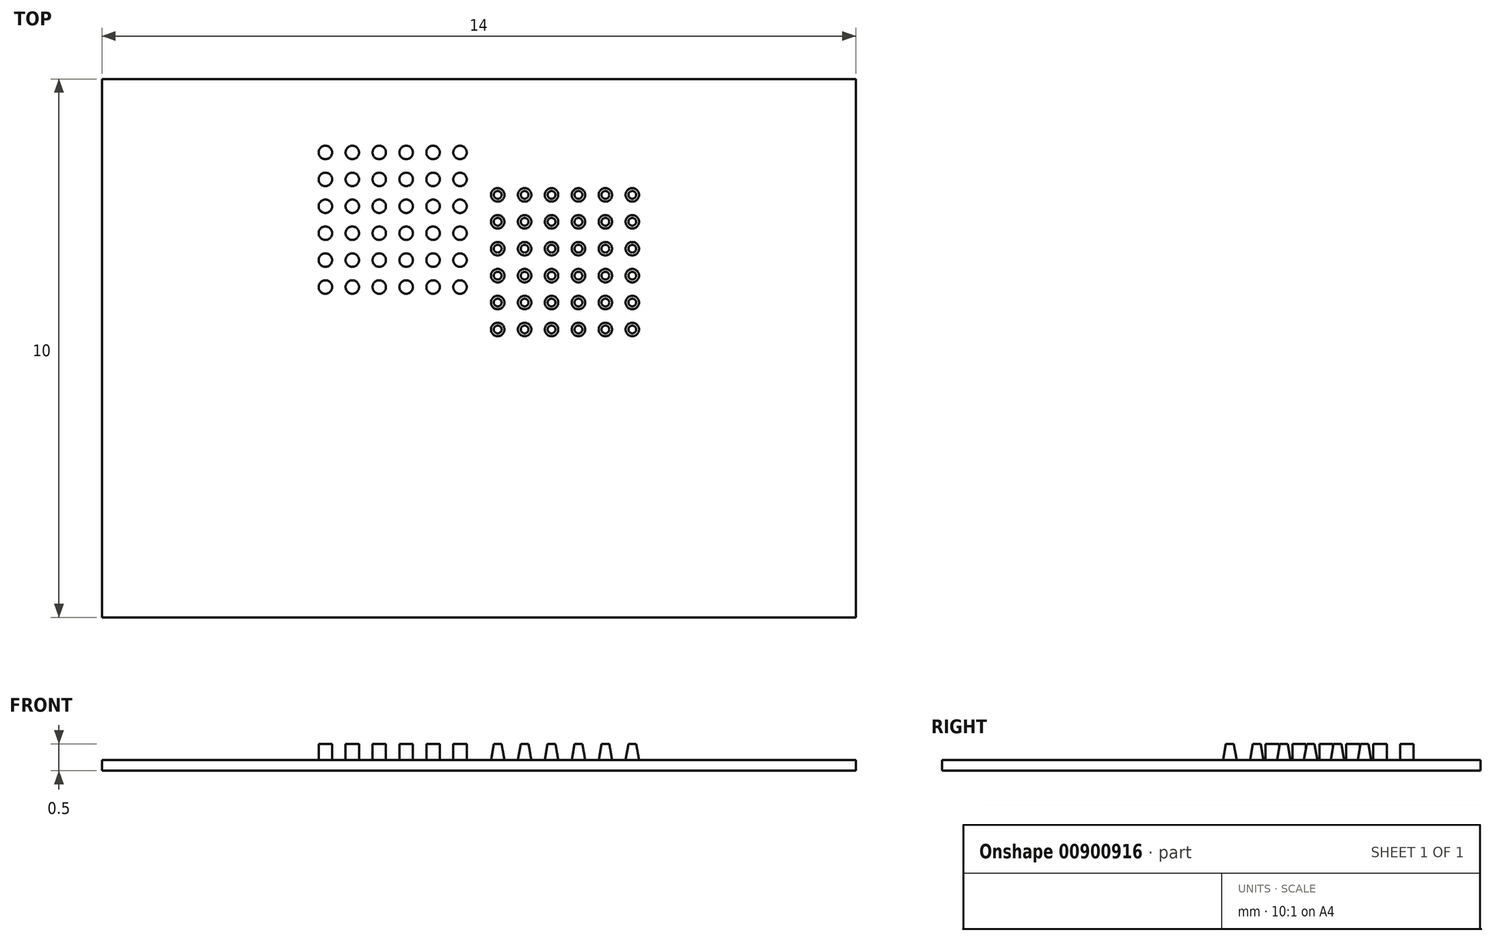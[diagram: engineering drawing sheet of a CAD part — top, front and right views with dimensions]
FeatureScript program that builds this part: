
annotation { "Feature Type Name" : "Feature", "Feature Type Description" : "" }
export const myFeature = defineFeature(function(context is Context, id is Id, definition is map)
    precondition{}
    {
        {
            var Q0;
            Q0=qCreatedBy(makeId("Top.planeOp"),FACE);
            var sketch = newSketch(context, id + "F0", { "sketchPlane" : qUnion([Q0])});
            skLineSegment(sketch, "E0.bottom", {"start": v(-7, -5) * mm, "end": v(7, -5) * mm});
            skLineSegment(sketch, "E0.top", {"start": v(-7, 5) * mm, "end": v(7, 5) * mm});
            skLineSegment(sketch, "E0.left", {"start": v(-7, -5) * mm, "end": v(-7, 5) * mm});
            skLineSegment(sketch, "E0.right", {"start": v(7, -5) * mm, "end": v(7, 5) * mm});
            skLineSegment(sketch, "E1", {"start": v(0, 5) * mm, "end": v(0, -5) * mm});
            skSolve(sketch);
        }
        {
            var Q0;
            Q0=qSketchRegion(id+"F0",true);
            extrude(context, id + "F1", {"entities" : qUnion([Q0]), "oppositeDirection" : true, "depth" : 0.2 * mm, "offsetDistance" : 25 * mm});
        }
        {
            var Q0;
            Q0=makeQuery(id+"F1.opExtrude","CAP_FACE",FACE,{"disambiguationData":[OSD([sQuery(id+"F0.wireOp",EDGE,"E0.bottom"),sQuery(id+"F0.wireOp",EDGE,"E0.top"),sQuery(id+"F0.wireOp",EDGE,"E0.left"),sQuery(id+"F0.wireOp",EDGE,"E0.right")])],"isStart":true});
            var sketch = newSketch(context, id + "F2", { "sketchPlane" : qUnion([Q0])});
            skCircle(sketch, "E2", {"center": v(-2.85, 1.14) * mm, "radius": 0.12 * mm});
            skCircle(sketch, "E3.0.1.0", {"center": v(-2.85, 1.64) * mm, "radius": 0.12 * mm});
            skCircle(sketch, "E3.0.2.0", {"center": v(-2.85, 2.14) * mm, "radius": 0.12 * mm});
            skCircle(sketch, "E3.0.3.0", {"center": v(-2.85, 2.64) * mm, "radius": 0.12 * mm});
            skCircle(sketch, "E3.0.4.0", {"center": v(-2.85, 3.14) * mm, "radius": 0.12 * mm});
            skCircle(sketch, "E3.0.5.0", {"center": v(-2.85, 3.64) * mm, "radius": 0.12 * mm});
            skCircle(sketch, "E3.1.0.0", {"center": v(-2.35, 1.14) * mm, "radius": 0.12 * mm});
            skCircle(sketch, "E3.1.1.0", {"center": v(-2.35, 1.64) * mm, "radius": 0.12 * mm});
            skCircle(sketch, "E3.1.2.0", {"center": v(-2.35, 2.14) * mm, "radius": 0.12 * mm});
            skCircle(sketch, "E3.1.3.0", {"center": v(-2.35, 2.64) * mm, "radius": 0.12 * mm});
            skCircle(sketch, "E3.1.4.0", {"center": v(-2.35, 3.14) * mm, "radius": 0.12 * mm});
            skCircle(sketch, "E3.1.5.0", {"center": v(-2.35, 3.64) * mm, "radius": 0.12 * mm});
            skCircle(sketch, "E3.2.0.0", {"center": v(-1.85, 1.14) * mm, "radius": 0.12 * mm});
            skCircle(sketch, "E3.2.1.0", {"center": v(-1.85, 1.64) * mm, "radius": 0.12 * mm});
            skCircle(sketch, "E3.2.2.0", {"center": v(-1.85, 2.14) * mm, "radius": 0.12 * mm});
            skCircle(sketch, "E3.2.3.0", {"center": v(-1.85, 2.64) * mm, "radius": 0.12 * mm});
            skCircle(sketch, "E3.2.4.0", {"center": v(-1.85, 3.14) * mm, "radius": 0.12 * mm});
            skCircle(sketch, "E3.2.5.0", {"center": v(-1.85, 3.64) * mm, "radius": 0.12 * mm});
            skCircle(sketch, "E3.3.0.0", {"center": v(-1.35, 1.14) * mm, "radius": 0.12 * mm});
            skCircle(sketch, "E3.3.1.0", {"center": v(-1.35, 1.64) * mm, "radius": 0.12 * mm});
            skCircle(sketch, "E3.3.2.0", {"center": v(-1.35, 2.14) * mm, "radius": 0.12 * mm});
            skCircle(sketch, "E3.3.3.0", {"center": v(-1.35, 2.64) * mm, "radius": 0.12 * mm});
            skCircle(sketch, "E3.3.4.0", {"center": v(-1.35, 3.14) * mm, "radius": 0.12 * mm});
            skCircle(sketch, "E3.3.5.0", {"center": v(-1.35, 3.64) * mm, "radius": 0.12 * mm});
            skCircle(sketch, "E3.4.0.0", {"center": v(-0.85, 1.14) * mm, "radius": 0.12 * mm});
            skCircle(sketch, "E3.4.1.0", {"center": v(-0.85, 1.64) * mm, "radius": 0.12 * mm});
            skCircle(sketch, "E3.4.2.0", {"center": v(-0.85, 2.14) * mm, "radius": 0.12 * mm});
            skCircle(sketch, "E3.4.3.0", {"center": v(-0.85, 2.64) * mm, "radius": 0.12 * mm});
            skCircle(sketch, "E3.4.4.0", {"center": v(-0.85, 3.14) * mm, "radius": 0.12 * mm});
            skCircle(sketch, "E3.4.5.0", {"center": v(-0.85, 3.64) * mm, "radius": 0.12 * mm});
            skCircle(sketch, "E3.5.0.0", {"center": v(-0.35, 1.14) * mm, "radius": 0.12 * mm});
            skCircle(sketch, "E3.5.1.0", {"center": v(-0.35, 1.64) * mm, "radius": 0.12 * mm});
            skCircle(sketch, "E3.5.2.0", {"center": v(-0.35, 2.14) * mm, "radius": 0.12 * mm});
            skCircle(sketch, "E3.5.3.0", {"center": v(-0.35, 2.64) * mm, "radius": 0.12 * mm});
            skCircle(sketch, "E3.5.4.0", {"center": v(-0.35, 3.14) * mm, "radius": 0.12 * mm});
            skCircle(sketch, "E3.5.5.0", {"center": v(-0.35, 3.64) * mm, "radius": 0.12 * mm});
            skLineSegment(sketch, "E3.direction1", {"start": v(-2.85, 1.14) * mm, "end": v(-2.35, 1.14) * mm, "construction": true});
            skLineSegment(sketch, "E3.direction2", {"start": v(-2.85, 1.14) * mm, "end": v(-2.85, 1.64) * mm, "construction": true});
            skSolve(sketch);
        }
        {
            var Q0;
            Q0=makeQuery(id+"F2.imprint","IMPRINT",FACE,{"disambiguationData":[TD([[makeQuery(id+"F2.imprint","IMPRINT",EDGE,{"derivedFrom":sQuery(id+"F2.wireOp",EDGE,"E3.4.2.0")}),1.0]])]});
            var sketch = newSketch(context, id + "F3", { "sketchPlane" : qUnion([Q0])});
            skCircle(sketch, "E4", {"center": v(0.35, 0.35) * mm, "radius": 0.12 * mm});
            skCircle(sketch, "E5.0.1.0", {"center": v(0.35, 0.85) * mm, "radius": 0.12 * mm});
            skCircle(sketch, "E5.0.2.0", {"center": v(0.35, 1.35) * mm, "radius": 0.12 * mm});
            skCircle(sketch, "E5.0.3.0", {"center": v(0.35, 1.85) * mm, "radius": 0.12 * mm});
            skCircle(sketch, "E5.0.4.0", {"center": v(0.35, 2.35) * mm, "radius": 0.12 * mm});
            skCircle(sketch, "E5.0.5.0", {"center": v(0.35, 2.85) * mm, "radius": 0.12 * mm});
            skCircle(sketch, "E5.1.0.0", {"center": v(0.85, 0.35) * mm, "radius": 0.12 * mm});
            skCircle(sketch, "E5.1.1.0", {"center": v(0.85, 0.85) * mm, "radius": 0.12 * mm});
            skCircle(sketch, "E5.1.2.0", {"center": v(0.85, 1.35) * mm, "radius": 0.12 * mm});
            skCircle(sketch, "E5.1.3.0", {"center": v(0.85, 1.85) * mm, "radius": 0.12 * mm});
            skCircle(sketch, "E5.1.4.0", {"center": v(0.85, 2.35) * mm, "radius": 0.12 * mm});
            skCircle(sketch, "E5.1.5.0", {"center": v(0.85, 2.85) * mm, "radius": 0.12 * mm});
            skCircle(sketch, "E5.2.0.0", {"center": v(1.35, 0.35) * mm, "radius": 0.12 * mm});
            skCircle(sketch, "E5.2.1.0", {"center": v(1.35, 0.85) * mm, "radius": 0.12 * mm});
            skCircle(sketch, "E5.2.2.0", {"center": v(1.35, 1.35) * mm, "radius": 0.12 * mm});
            skCircle(sketch, "E5.2.3.0", {"center": v(1.35, 1.85) * mm, "radius": 0.12 * mm});
            skCircle(sketch, "E5.2.4.0", {"center": v(1.35, 2.35) * mm, "radius": 0.12 * mm});
            skCircle(sketch, "E5.2.5.0", {"center": v(1.35, 2.85) * mm, "radius": 0.12 * mm});
            skCircle(sketch, "E5.3.0.0", {"center": v(1.85, 0.35) * mm, "radius": 0.12 * mm});
            skCircle(sketch, "E5.3.1.0", {"center": v(1.85, 0.85) * mm, "radius": 0.12 * mm});
            skCircle(sketch, "E5.3.2.0", {"center": v(1.85, 1.35) * mm, "radius": 0.12 * mm});
            skCircle(sketch, "E5.3.3.0", {"center": v(1.85, 1.85) * mm, "radius": 0.12 * mm});
            skCircle(sketch, "E5.3.4.0", {"center": v(1.85, 2.35) * mm, "radius": 0.12 * mm});
            skCircle(sketch, "E5.3.5.0", {"center": v(1.85, 2.85) * mm, "radius": 0.12 * mm});
            skCircle(sketch, "E5.4.0.0", {"center": v(2.35, 0.35) * mm, "radius": 0.12 * mm});
            skCircle(sketch, "E5.4.1.0", {"center": v(2.35, 0.85) * mm, "radius": 0.12 * mm});
            skCircle(sketch, "E5.4.2.0", {"center": v(2.35, 1.35) * mm, "radius": 0.12 * mm});
            skCircle(sketch, "E5.4.3.0", {"center": v(2.35, 1.85) * mm, "radius": 0.12 * mm});
            skCircle(sketch, "E5.4.4.0", {"center": v(2.35, 2.35) * mm, "radius": 0.12 * mm});
            skCircle(sketch, "E5.4.5.0", {"center": v(2.35, 2.85) * mm, "radius": 0.12 * mm});
            skCircle(sketch, "E5.5.0.0", {"center": v(2.85, 0.35) * mm, "radius": 0.12 * mm});
            skCircle(sketch, "E5.5.1.0", {"center": v(2.85, 0.85) * mm, "radius": 0.12 * mm});
            skCircle(sketch, "E5.5.2.0", {"center": v(2.85, 1.35) * mm, "radius": 0.12 * mm});
            skCircle(sketch, "E5.5.3.0", {"center": v(2.85, 1.85) * mm, "radius": 0.12 * mm});
            skCircle(sketch, "E5.5.4.0", {"center": v(2.85, 2.35) * mm, "radius": 0.12 * mm});
            skCircle(sketch, "E5.5.5.0", {"center": v(2.85, 2.85) * mm, "radius": 0.12 * mm});
            skLineSegment(sketch, "E5.direction1", {"start": v(0.35, 0.35) * mm, "end": v(0.85, 0.35) * mm, "construction": true});
            skLineSegment(sketch, "E5.direction2", {"start": v(0.35, 0.35) * mm, "end": v(0.35, 0.85) * mm, "construction": true});
            skSolve(sketch);
        }
        {
            var Q0;
            Q0=makeQuery(id+"F2.imprint","IMPRINT",FACE,{"disambiguationData":[TD([[makeQuery(id+"F2.imprint","IMPRINT",EDGE,{"derivedFrom":sQuery(id+"F2.wireOp",EDGE,"E3.3.2.0")}),1.0]])]});
            var Q1;
            Q1=makeQuery(id+"F2.imprint","IMPRINT",FACE,{"disambiguationData":[TD([[makeQuery(id+"F2.imprint","IMPRINT",EDGE,{"derivedFrom":sQuery(id+"F2.wireOp",EDGE,"E3.4.5.0")}),1.0]])]});
            var Q2;
            Q2=makeQuery(id+"F2.imprint","IMPRINT",FACE,{"disambiguationData":[TD([[makeQuery(id+"F2.imprint","IMPRINT",EDGE,{"derivedFrom":sQuery(id+"F2.wireOp",EDGE,"E3.4.2.0")}),1.0]])]});
            var Q3;
            Q3=makeQuery(id+"F2.imprint","IMPRINT",FACE,{"disambiguationData":[TD([[makeQuery(id+"F2.imprint","IMPRINT",EDGE,{"derivedFrom":sQuery(id+"F2.wireOp",EDGE,"E3.5.5.0")}),1.0]])]});
            var Q4;
            Q4=makeQuery(id+"F2.imprint","IMPRINT",FACE,{"disambiguationData":[TD([[makeQuery(id+"F2.imprint","IMPRINT",EDGE,{"derivedFrom":sQuery(id+"F2.wireOp",EDGE,"E3.3.1.0")}),1.0]])]});
            var Q5;
            Q5=makeQuery(id+"F2.imprint","IMPRINT",FACE,{"disambiguationData":[TD([[makeQuery(id+"F2.imprint","IMPRINT",EDGE,{"derivedFrom":sQuery(id+"F2.wireOp",EDGE,"E3.2.0.0")}),1.0]])]});
            var Q6;
            Q6=makeQuery(id+"F2.imprint","IMPRINT",FACE,{"disambiguationData":[TD([[makeQuery(id+"F2.imprint","IMPRINT",EDGE,{"derivedFrom":sQuery(id+"F2.wireOp",EDGE,"E3.4.1.0")}),1.0]])]});
            var Q7;
            Q7=makeQuery(id+"F2.imprint","IMPRINT",FACE,{"disambiguationData":[TD([[makeQuery(id+"F2.imprint","IMPRINT",EDGE,{"derivedFrom":sQuery(id+"F2.wireOp",EDGE,"E3.0.4.0")}),1.0]])]});
            var Q8;
            Q8=makeQuery(id+"F2.imprint","IMPRINT",FACE,{"disambiguationData":[TD([[makeQuery(id+"F2.imprint","IMPRINT",EDGE,{"derivedFrom":sQuery(id+"F2.wireOp",EDGE,"E3.0.5.0")}),1.0]])]});
            var Q9;
            Q9=makeQuery(id+"F2.imprint","IMPRINT",FACE,{"disambiguationData":[TD([[makeQuery(id+"F2.imprint","IMPRINT",EDGE,{"derivedFrom":sQuery(id+"F2.wireOp",EDGE,"E3.4.0.0")}),1.0]])]});
            var Q10;
            Q10=makeQuery(id+"F2.imprint","IMPRINT",FACE,{"disambiguationData":[TD([[makeQuery(id+"F2.imprint","IMPRINT",EDGE,{"derivedFrom":sQuery(id+"F2.wireOp",EDGE,"E2")}),1.0]])]});
            var Q11;
            Q11=makeQuery(id+"F2.imprint","IMPRINT",FACE,{"disambiguationData":[TD([[makeQuery(id+"F2.imprint","IMPRINT",EDGE,{"derivedFrom":sQuery(id+"F2.wireOp",EDGE,"E3.2.2.0")}),1.0]])]});
            var Q12;
            Q12=makeQuery(id+"F2.imprint","IMPRINT",FACE,{"disambiguationData":[TD([[makeQuery(id+"F2.imprint","IMPRINT",EDGE,{"derivedFrom":sQuery(id+"F2.wireOp",EDGE,"E3.0.2.0")}),1.0]])]});
            var Q13;
            Q13=makeQuery(id+"F2.imprint","IMPRINT",FACE,{"disambiguationData":[TD([[makeQuery(id+"F2.imprint","IMPRINT",EDGE,{"derivedFrom":sQuery(id+"F2.wireOp",EDGE,"E3.1.0.0")}),1.0]])]});
            var Q14;
            Q14=makeQuery(id+"F2.imprint","IMPRINT",FACE,{"disambiguationData":[TD([[makeQuery(id+"F2.imprint","IMPRINT",EDGE,{"derivedFrom":sQuery(id+"F2.wireOp",EDGE,"E3.3.0.0")}),1.0]])]});
            var Q15;
            Q15=makeQuery(id+"F2.imprint","IMPRINT",FACE,{"disambiguationData":[TD([[makeQuery(id+"F2.imprint","IMPRINT",EDGE,{"derivedFrom":sQuery(id+"F2.wireOp",EDGE,"E3.5.4.0")}),1.0]])]});
            var Q16;
            Q16=makeQuery(id+"F2.imprint","IMPRINT",FACE,{"disambiguationData":[TD([[makeQuery(id+"F2.imprint","IMPRINT",EDGE,{"derivedFrom":sQuery(id+"F2.wireOp",EDGE,"E3.1.5.0")}),1.0]])]});
            var Q17;
            Q17=makeQuery(id+"F2.imprint","IMPRINT",FACE,{"disambiguationData":[TD([[makeQuery(id+"F2.imprint","IMPRINT",EDGE,{"derivedFrom":sQuery(id+"F2.wireOp",EDGE,"E3.2.1.0")}),1.0]])]});
            var Q18;
            Q18=makeQuery(id+"F2.imprint","IMPRINT",FACE,{"disambiguationData":[TD([[makeQuery(id+"F2.imprint","IMPRINT",EDGE,{"derivedFrom":sQuery(id+"F2.wireOp",EDGE,"E3.1.4.0")}),1.0]])]});
            var Q19;
            Q19=makeQuery(id+"F2.imprint","IMPRINT",FACE,{"disambiguationData":[TD([[makeQuery(id+"F2.imprint","IMPRINT",EDGE,{"derivedFrom":sQuery(id+"F2.wireOp",EDGE,"E3.1.3.0")}),1.0]])]});
            var Q20;
            Q20=makeQuery(id+"F2.imprint","IMPRINT",FACE,{"disambiguationData":[TD([[makeQuery(id+"F2.imprint","IMPRINT",EDGE,{"derivedFrom":sQuery(id+"F2.wireOp",EDGE,"E3.5.1.0")}),1.0]])]});
            var Q21;
            Q21=makeQuery(id+"F2.imprint","IMPRINT",FACE,{"disambiguationData":[TD([[makeQuery(id+"F2.imprint","IMPRINT",EDGE,{"derivedFrom":sQuery(id+"F2.wireOp",EDGE,"E3.1.2.0")}),1.0]])]});
            var Q22;
            Q22=makeQuery(id+"F2.imprint","IMPRINT",FACE,{"disambiguationData":[TD([[makeQuery(id+"F2.imprint","IMPRINT",EDGE,{"derivedFrom":sQuery(id+"F2.wireOp",EDGE,"E3.1.1.0")}),1.0]])]});
            var Q23;
            Q23=makeQuery(id+"F2.imprint","IMPRINT",FACE,{"disambiguationData":[TD([[makeQuery(id+"F2.imprint","IMPRINT",EDGE,{"derivedFrom":sQuery(id+"F2.wireOp",EDGE,"E3.0.3.0")}),1.0]])]});
            var Q24;
            Q24=makeQuery(id+"F2.imprint","IMPRINT",FACE,{"disambiguationData":[TD([[makeQuery(id+"F2.imprint","IMPRINT",EDGE,{"derivedFrom":sQuery(id+"F2.wireOp",EDGE,"E3.0.1.0")}),1.0]])]});
            var Q25;
            Q25=makeQuery(id+"F2.imprint","IMPRINT",FACE,{"disambiguationData":[TD([[makeQuery(id+"F2.imprint","IMPRINT",EDGE,{"derivedFrom":sQuery(id+"F2.wireOp",EDGE,"E3.2.3.0")}),1.0]])]});
            var Q26;
            Q26=makeQuery(id+"F2.imprint","IMPRINT",FACE,{"disambiguationData":[TD([[makeQuery(id+"F2.imprint","IMPRINT",EDGE,{"derivedFrom":sQuery(id+"F2.wireOp",EDGE,"E3.4.3.0")}),1.0]])]});
            var Q27;
            Q27=makeQuery(id+"F2.imprint","IMPRINT",FACE,{"disambiguationData":[TD([[makeQuery(id+"F2.imprint","IMPRINT",EDGE,{"derivedFrom":sQuery(id+"F2.wireOp",EDGE,"E3.5.0.0")}),1.0]])]});
            var Q28;
            Q28=makeQuery(id+"F2.imprint","IMPRINT",FACE,{"disambiguationData":[TD([[makeQuery(id+"F2.imprint","IMPRINT",EDGE,{"derivedFrom":sQuery(id+"F2.wireOp",EDGE,"E3.3.3.0")}),1.0]])]});
            var Q29;
            Q29=makeQuery(id+"F2.imprint","IMPRINT",FACE,{"disambiguationData":[TD([[makeQuery(id+"F2.imprint","IMPRINT",EDGE,{"derivedFrom":sQuery(id+"F2.wireOp",EDGE,"E3.4.4.0")}),1.0]])]});
            var Q30;
            Q30=makeQuery(id+"F2.imprint","IMPRINT",FACE,{"disambiguationData":[TD([[makeQuery(id+"F2.imprint","IMPRINT",EDGE,{"derivedFrom":sQuery(id+"F2.wireOp",EDGE,"E3.3.4.0")}),1.0]])]});
            var Q31;
            Q31=makeQuery(id+"F2.imprint","IMPRINT",FACE,{"disambiguationData":[TD([[makeQuery(id+"F2.imprint","IMPRINT",EDGE,{"derivedFrom":sQuery(id+"F2.wireOp",EDGE,"E3.5.2.0")}),1.0]])]});
            var Q32;
            Q32=makeQuery(id+"F2.imprint","IMPRINT",FACE,{"disambiguationData":[TD([[makeQuery(id+"F2.imprint","IMPRINT",EDGE,{"derivedFrom":sQuery(id+"F2.wireOp",EDGE,"E3.2.4.0")}),1.0]])]});
            var Q33;
            Q33=makeQuery(id+"F2.imprint","IMPRINT",FACE,{"disambiguationData":[TD([[makeQuery(id+"F2.imprint","IMPRINT",EDGE,{"derivedFrom":sQuery(id+"F2.wireOp",EDGE,"E3.3.5.0")}),1.0]])]});
            var Q34;
            Q34=makeQuery(id+"F2.imprint","IMPRINT",FACE,{"disambiguationData":[TD([[makeQuery(id+"F2.imprint","IMPRINT",EDGE,{"derivedFrom":sQuery(id+"F2.wireOp",EDGE,"E3.5.3.0")}),1.0]])]});
            var Q35;
            Q35=makeQuery(id+"F2.imprint","IMPRINT",FACE,{"disambiguationData":[TD([[makeQuery(id+"F2.imprint","IMPRINT",EDGE,{"derivedFrom":sQuery(id+"F2.wireOp",EDGE,"E3.2.5.0")}),1.0]])]});
            var Q36;
            Q36=makeQuery(id+"F3.imprint","IMPRINT",FACE,{"disambiguationData":[TD([[makeQuery(id+"F3.imprint","IMPRINT",EDGE,{"derivedFrom":makeQuery(id+"F2.imprint","IMPRINT",EDGE,{"derivedFrom":sQuery(id+"F2.wireOp",EDGE,"E3.4.2.0")})}),1.0]])]});
            extrude(context, id + "F4", {"entities" : qUnion([Q0, Q1, Q2, Q3, Q4, Q5, Q6, Q7, Q8, Q9, Q10, Q11, Q12, Q13, Q14, Q15, Q16, Q17, Q18, Q19, Q20, Q21, Q22, Q23, Q24, Q25, Q26, Q27, Q28, Q29, Q30, Q31, Q32, Q33, Q34, Q35, Q36]), "operationType" : NewBodyOperationType.ADD, "depth" : 0.3 * mm, "offsetDistance" : 25 * mm});
        }
        {
            var Q0;
            Q0=qSketchRegion(id+"F3",true);
            extrude(context, id + "F5", {"entities" : qUnion([Q0]), "operationType" : NewBodyOperationType.ADD, "depth" : 0.3 * mm, "offsetDistance" : 25 * mm, "hasDraft" : true, "draftAngle" : 10 * degree, "draftPullDirection" : true});
        }
    });
